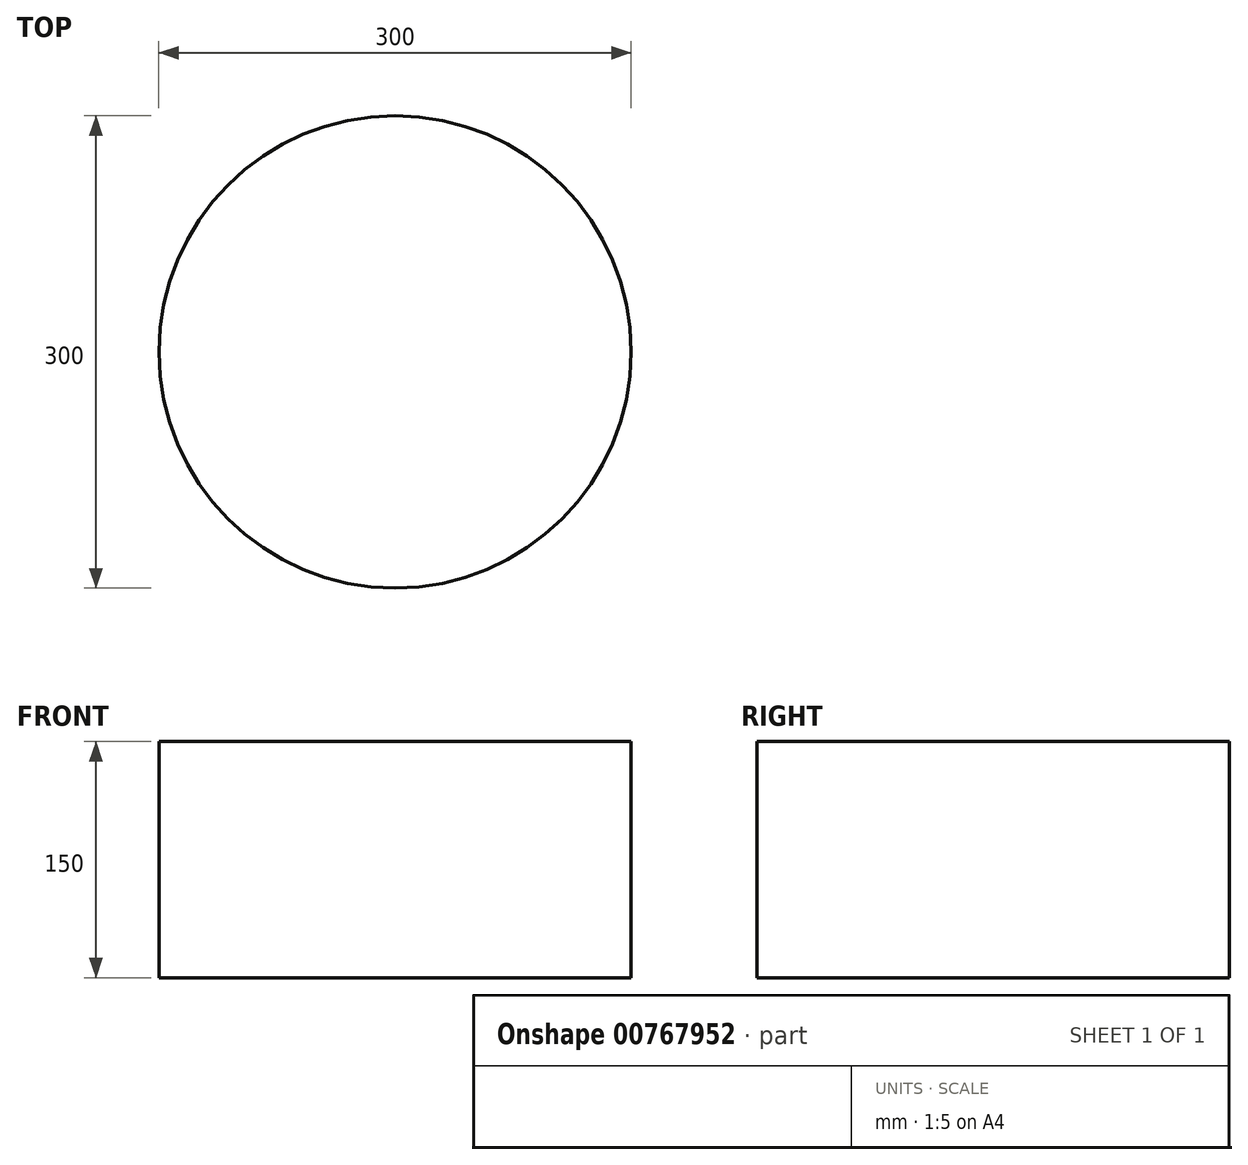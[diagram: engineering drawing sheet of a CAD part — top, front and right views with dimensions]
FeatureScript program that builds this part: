
annotation { "Feature Type Name" : "Feature", "Feature Type Description" : "" }
export const myFeature = defineFeature(function(context is Context, id is Id, definition is map)
    precondition{}
    {
        {
            var Q0;
            Q0=qCreatedBy(makeId("Top.planeOp"),FACE);
            var sketch = newSketch(context, id + "F0", { "sketchPlane" : qUnion([Q0])});
            skCircle(sketch, "E0", {"center": v(-0.69, 0.83) * mm, "radius": 150 * mm});
            skSolve(sketch);
        }
        {
            var Q0;
            Q0=makeQuery(id+"F0.imprint","IMPRINT",FACE,{"disambiguationData":[TD([[makeQuery(id+"F0.imprint","IMPRINT",EDGE,{"derivedFrom":sQuery(id+"F0.wireOp",EDGE,"E0")}),1.0]])]});
            extrude(context, id + "F1", {"entities" : qUnion([Q0]), "depth" : 150 * mm, "offsetDistance" : 25 * mm});
        }
    });
